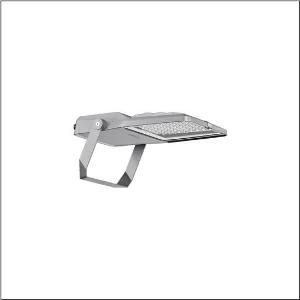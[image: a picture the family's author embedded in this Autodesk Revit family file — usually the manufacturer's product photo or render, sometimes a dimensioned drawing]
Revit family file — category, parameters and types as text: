
# Revit family: floodlight_fl_21_mini___pl33t_5xa7775c2f1a_de84
name_source: partatom
category: Lighting Fixtures
units: mm (PartAtom-declared; Revit-internal decimal feet)

## family parameters
Cut with Voids When Loaded = No
Host = Face
Light Source = No
Part Type = Normal
Room Calculation Point = No
Round Connector Dimension = Use Diameter
Shared = No

## types (1)
- --- (1 x LED, 12050 lm, 89 W, 3000K)
    Apparent Load = 89 VA
    CIE Flux Codes = 26 75 99 100 100
    Color Rendering = 70
    Color Temperature = 3000K
    Default Elevation = 1800 mm
    Description = Floodlight FL 21 mini, floodlight, primary light control with lens, of PMMA, primary optical cover: protective disc, of toughened safety glass, transparent, light distribution: PL33T, light emission: direct distribution, installation type: surface-mounted, LED, High Power LED, rated luminous flux: 12.050lm, luminous efficacy: 135lm/W, light colour: 730, colour temperature: 3000K, control gear: Smart Interface (Zhaga), control: flexible luminous flux parameterisation, time-dependent luminous flux control, constant luminous flux control, overheat protection, pre-setting: logarithmic dimming characteristic, with terminal, 6-pole, mains connection: 220..240V, AC, 50/60Hz, start of lifetime: 89W, end of service life: 94W, reduction: 43W, luminaire housing, of diecast aluminium, powder-coated, SITECO metallic grey (DB 702S), corrosivity category C5 mid according to DIN EN ISO 12944, suitable for swimming pools, chlorine-resistant, sealing non-destructively replaceable, mounting bracket, of steel, galvanised, powder-coated, SITECO metallic grey (DB 702S), Smart Interface above, protection rating (complete): IP66, insulation class (complete): insulation class II (safety insulation), certification: CE, ENEC, VDE, protection symbol: D, impact resistance: IK08, permissible operating ambient temperature: -40..+40°C, permissible operating ambient temperature for outdoor applications: -40..+50°C, standard: DIN EN 12944, LABS conformity tested according to VDMA 24364:2018-05, packaging unit: 1 piece

Light Distribution: PL33T
    Height = 70 mm
    Lamp = 1 x LED
    Lamp Light Flux = 12050 lm
    Lamp Power = 89 W
    Lamp count = 1
    Length = 485 mm
    Luminous efficacy = 135 lm/W
    Manufacturer = Siteco
    ModVariant = No
    Model = 5XA7775C2F1A
    Mounting Place = Pole
    Mounting Type = Pole annexe
    Number of Poles = 1
    OnlyDefault = Yes
    Power Factor = 1
    Product Name = Floodlight FL 21 mini | PL33T
    Product group = floodlight | pylon annexe
    ProductGroupID = 6201
    Protection Class = Protection class II
    Protection Degree = IP 66
    RLX_Detail_Level = 1
    RLX_Emergency_Light_Flux = 0 lm
    RLX_Emergency_Type = 0
    RLX_Emergency_Type_DB = No
    RlxData = <blob elided: 95917 chars, md5=60d8bab1>
    Socket = socket
    Standby Power = 0 W
    System Light Flux = 12050 lm
    System Power = 89 W
    Type Comments = factory setting: luminous flux: 100 % | dim-lin: 254 | 456 mA
    Type Image = l_1006845.jpg
    URL = http://relux.com
    VarID = @adj_149623
    Voltage = 0 V
    Weight = 0.00 kg
    Width = 337 mm

## geometry (parser evidence)
native form markers: Blend x4, Sweep x13
no freeform markers — native parametric forms only
